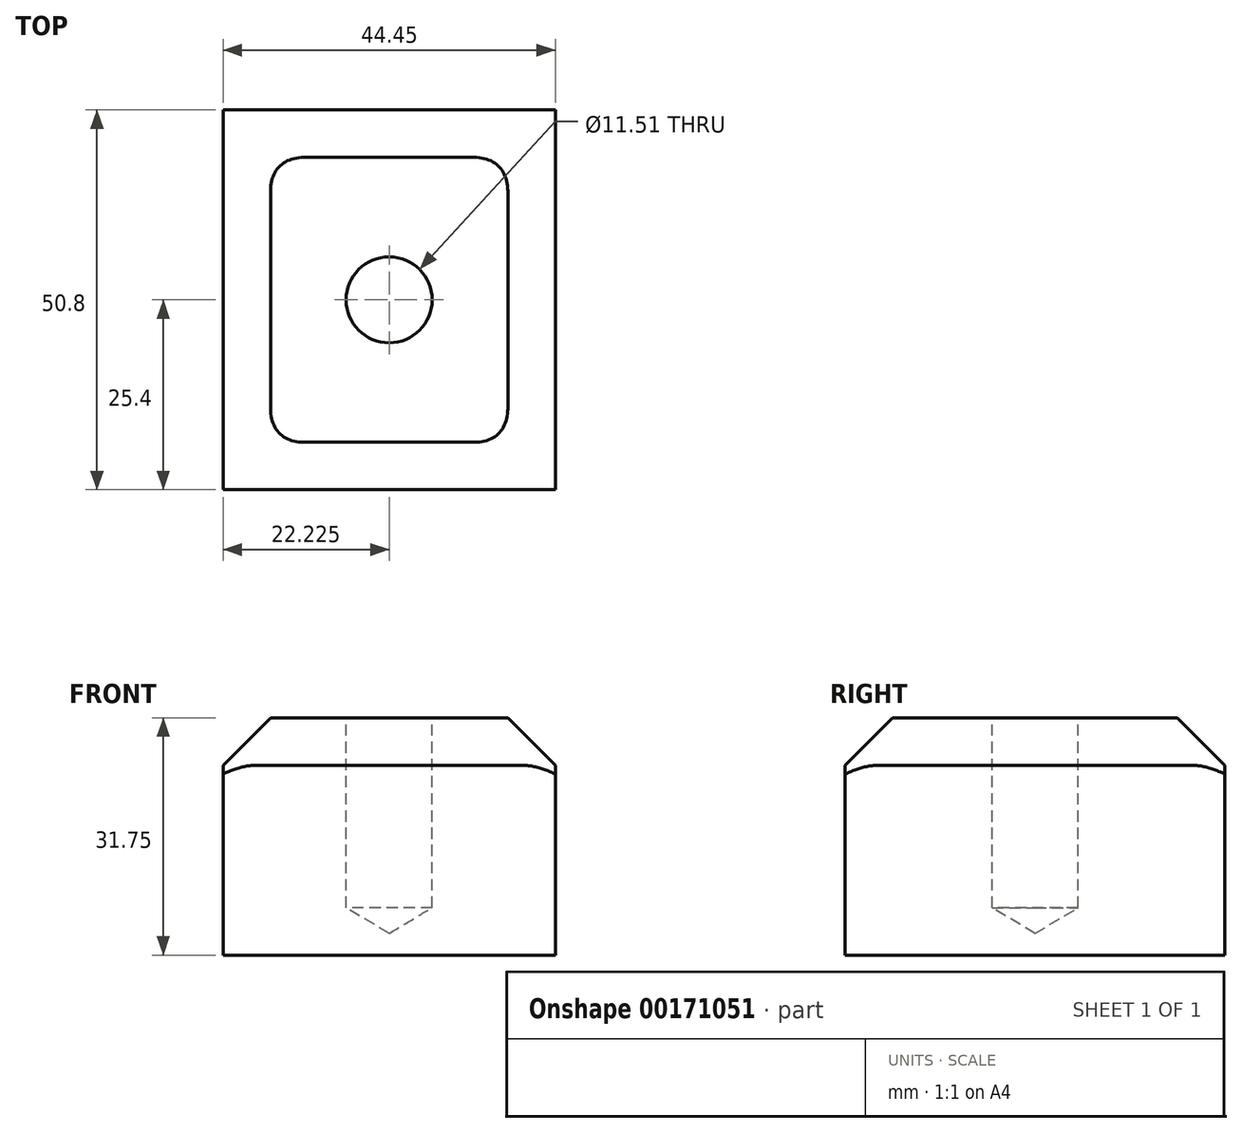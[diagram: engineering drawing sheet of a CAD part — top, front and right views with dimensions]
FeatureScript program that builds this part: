
annotation { "Feature Type Name" : "Feature", "Feature Type Description" : "" }
export const myFeature = defineFeature(function(context is Context, id is Id, definition is map)
    precondition{}
    {
        {
            var Q0;
            Q0=qCreatedBy(makeId("Front.planeOp"),FACE);
            var sketch = newSketch(context, id + "F0", { "sketchPlane" : qUnion([Q0])});
            skLineSegment(sketch, "E0", {"start": v(0, 0) * mm, "end": v(0, 31.75) * mm});
            skLineSegment(sketch, "E1", {"start": v(0, 31.75) * mm, "end": v(44.45, 31.75) * mm});
            skLineSegment(sketch, "E2", {"start": v(44.45, 31.75) * mm, "end": v(44.45, 0) * mm});
            skLineSegment(sketch, "E3", {"start": v(44.45, 0) * mm, "end": v(0, 0) * mm});
            skSolve(sketch);
        }
        {
            var Q0;
            Q0 = qSketchRegion(id + "F0", true);
            extrude(context, id + "F1", {"entities" : qUnion([Q0]), "depth" : 50.8 * mm});
        }
        {
            var Q0;
            Q0=makeQuery(id+"F1.opExtrude","SWEPT_FACE",FACE,{"disambiguationData":[OSD([sQuery(id+"F0.wireOp",EDGE,"E1")])]});
            var sketch = newSketch(context, id + "F2", { "sketchPlane" : qUnion([Q0])});
            skCircle(sketch, "E4", {"center": v(22.23, -25.4) * mm, "radius": 6.35 * mm});
            skSolve(sketch);
        }
        {
            var Q0;
            Q0=makeQuery(id+"F1.opExtrude","SWEPT_EDGE",EDGE,{"disambiguationData":[OSD([sQuery(id+"F0.wireOp",EDGE,"E0"),sQuery(id+"F0.wireOp",EDGE,"E1")])]});
            var Q1;
            Q1=makeQuery(id+"F1.opExtrude","CAP_EDGE",EDGE,{"disambiguationData":[OSD([sQuery(id+"F0.wireOp",EDGE,"E1")])],"isStart":false});
            var Q2;
            Q2=makeQuery(id+"F1.opExtrude","SWEPT_EDGE",EDGE,{"disambiguationData":[OSD([sQuery(id+"F0.wireOp",EDGE,"E1"),sQuery(id+"F0.wireOp",EDGE,"E2")])]});
            var Q3;
            Q3=makeQuery(id+"F1.opExtrude","CAP_EDGE",EDGE,{"disambiguationData":[OSD([sQuery(id+"F0.wireOp",EDGE,"E1")])],"isStart":true});
            chamfer(context, id + "F3", {"entities" : qUnion([Q0, Q1, Q2, Q3]), "chamferType" : ChamferType.OFFSET_ANGLE, "width" : 6.35 * mm, "oppositeDirection" : false, "angle" : 45 * degree, "tangentPropagation" : true});
        }
        {
            var Q0;
            {var subQ0=sQuery(id+"F0.wireOp",EDGE,"E1");Q0=makeQuery(id+"F3.opChamfer","BLEND_EDGE",EDGE,{"blendedFrom":[makeQuery(id+"F1.opExtrude","SWEPT_EDGE",EDGE,{"disambiguationData":[OSD([subQ0,sQuery(id+"F0.wireOp",EDGE,"E2")])]}),makeQuery(id+"F1.opExtrude","CAP_EDGE",EDGE,{"disambiguationData":[OSD([subQ0])],"isStart":false})],"blendedInto":[]});}
            var Q1;
            {var subQ0=sQuery(id+"F0.wireOp",EDGE,"E1");Q1=makeQuery(id+"F3.opChamfer","BLEND_EDGE",EDGE,{"blendedFrom":[makeQuery(id+"F1.opExtrude","SWEPT_EDGE",EDGE,{"disambiguationData":[OSD([subQ0,sQuery(id+"F0.wireOp",EDGE,"E2")])]}),makeQuery(id+"F1.opExtrude","CAP_EDGE",EDGE,{"disambiguationData":[OSD([subQ0])],"isStart":true})],"blendedInto":[]});}
            var Q2;
            {var subQ0=sQuery(id+"F0.wireOp",EDGE,"E1");Q2=makeQuery(id+"F3.opChamfer","BLEND_EDGE",EDGE,{"blendedFrom":[makeQuery(id+"F1.opExtrude","SWEPT_EDGE",EDGE,{"disambiguationData":[OSD([sQuery(id+"F0.wireOp",EDGE,"E0"),subQ0])]}),makeQuery(id+"F1.opExtrude","CAP_EDGE",EDGE,{"disambiguationData":[OSD([subQ0])],"isStart":true})],"blendedInto":[]});}
            var Q3;
            {var subQ0=sQuery(id+"F0.wireOp",EDGE,"E1");Q3=makeQuery(id+"F3.opChamfer","BLEND_EDGE",EDGE,{"blendedFrom":[makeQuery(id+"F1.opExtrude","SWEPT_EDGE",EDGE,{"disambiguationData":[OSD([sQuery(id+"F0.wireOp",EDGE,"E0"),subQ0])]}),makeQuery(id+"F1.opExtrude","CAP_EDGE",EDGE,{"disambiguationData":[OSD([subQ0])],"isStart":false})],"blendedInto":[]});}
            fillet(context, id + "F4", {"entities" : qUnion([Q0, Q1, Q2, Q3]), "radius" : 6.35 * mm, "tangentPropagation" : true, "allowEdgeOverflow" : false});
        }
        {
            var Q0;
            Q0=sQuery(id+"F2.wireOp",VERTEX,"E4.center");
            var Q1;
            Q1=makeQuery(id+"F1.opExtrude","SWEPT_BODY",BODY,{"disambiguationData":[OSD([sQuery(id+"F0.wireOp",EDGE,"E0"),sQuery(id+"F0.wireOp",EDGE,"E1"),sQuery(id+"F0.wireOp",EDGE,"E2"),sQuery(id+"F0.wireOp",EDGE,"E3")])]});
            hole(context, id + "F5", {"style" : HoleStyle.SIMPLE, "endStyle" : HoleEndStyle.BLIND, "standardTappedOrClearance" : lookupTablePath({ "standard" : "ANSI", "engagement" : "75%", "pitch" : "20 tpi", "size" : "1/2", "type" : "Tapped" }), "standardBlindInLast" : lookupTablePath({ "standard" : "ANSI", "engagement" : "75%", "pitch" : "20 tpi", "size" : "1/2", "type" : "Tapped" }), "holeDiameter" : 11.5 * mm, "holeDepth" : 25.4 * mm, "startFromSketch" : true, "locations" : qUnion([Q0]), "scope" : qUnion([Q1]), "majorDiameter" : 12.7 * mm});
        }
    });
